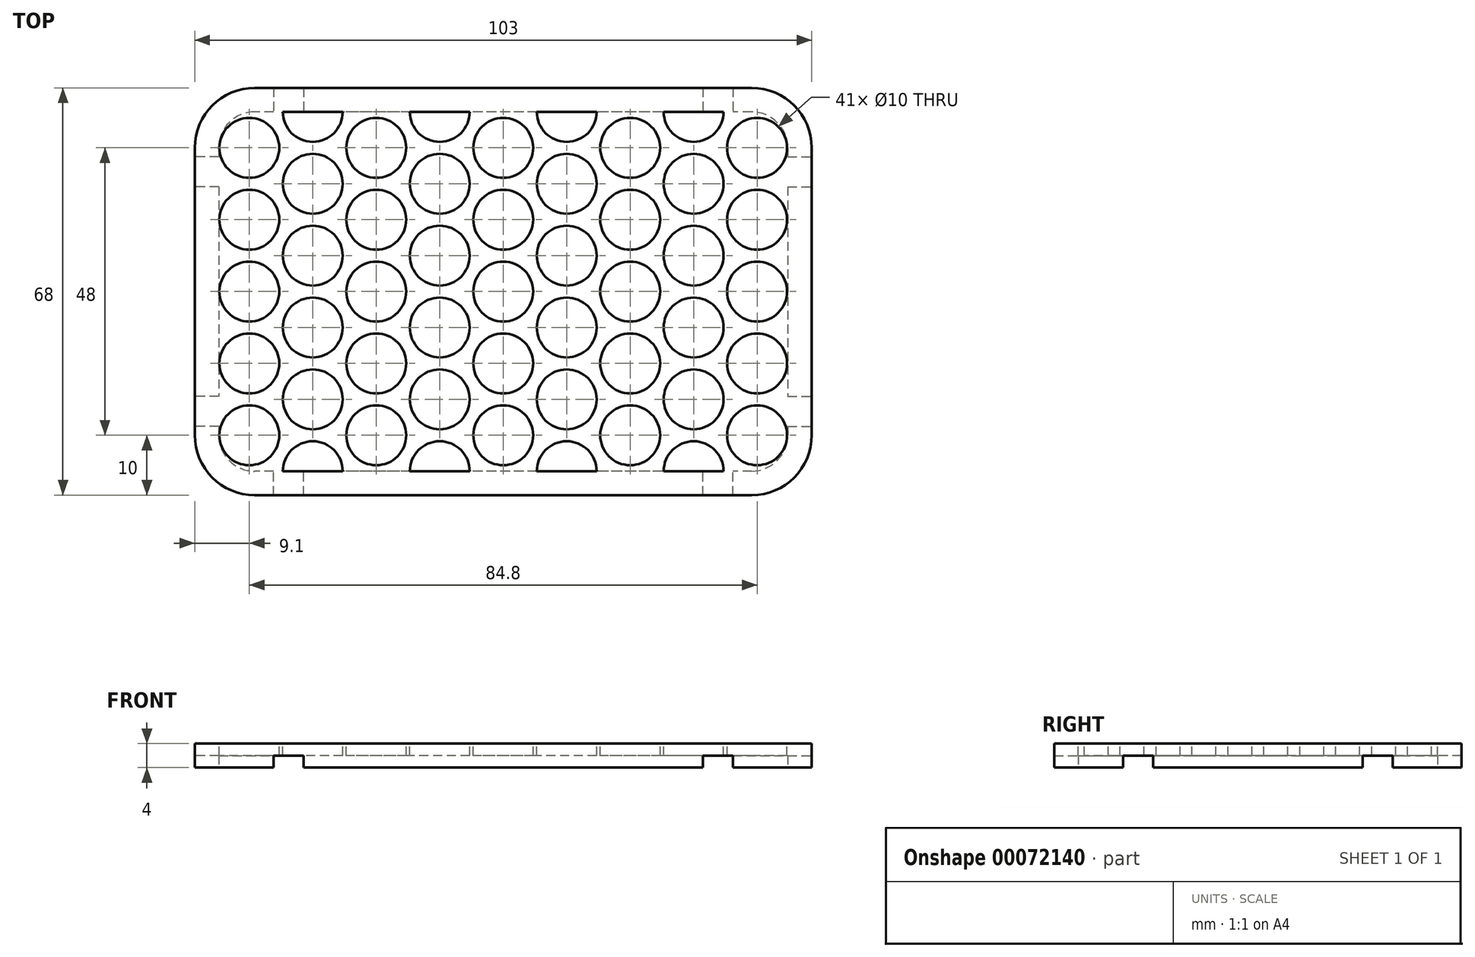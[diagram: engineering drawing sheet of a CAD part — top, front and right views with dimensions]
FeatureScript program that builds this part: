
annotation { "Feature Type Name" : "Feature", "Feature Type Description" : "" }
export const myFeature = defineFeature(function(context is Context, id is Id, definition is map)
    precondition{}
    {
        {
            var Q0;
            Q0=qCreatedBy(makeId("Top.planeOp"),FACE);
            var sketch = newSketch(context, id + "F0", { "sketchPlane" : qUnion([Q0])});
            skLineSegment(sketch, "E0.rect.bottom", {"start": v(41.5, 34) * mm, "end": v(-41.5, 34) * mm});
            skLineSegment(sketch, "E0.rect.top", {"start": v(41.5, -34) * mm, "end": v(-41.5, -34) * mm});
            skLineSegment(sketch, "E0.rect.left", {"start": v(51.5, 24) * mm, "end": v(51.5, -24) * mm});
            skLineSegment(sketch, "E0.rect.right", {"start": v(-51.5, 24) * mm, "end": v(-51.5, -24) * mm});
            skPoint(sketch, "E0.rect.middle", {"position": v(0, 0) * mm});
            skPoint(sketch, "E1.visualSharp", {"position": v(-51.5, 34) * mm});
            skArc(sketch, "E1.filletArc", {"start": v(-41.5, 34) * mm, "mid": v(-48.57, 31.07) * mm, "end": v(-51.5, 24) * mm});
            skPoint(sketch, "E2.visualSharp", {"position": v(51.5, 34) * mm});
            skArc(sketch, "E2.filletArc", {"start": v(51.5, 24) * mm, "mid": v(48.57, 31.07) * mm, "end": v(41.5, 34) * mm});
            skPoint(sketch, "E3.visualSharp", {"position": v(51.5, -34) * mm});
            skArc(sketch, "E3.filletArc", {"start": v(41.5, -34) * mm, "mid": v(48.57, -31.07) * mm, "end": v(51.5, -24) * mm});
            skPoint(sketch, "E4.visualSharp", {"position": v(-51.5, -34) * mm});
            skArc(sketch, "E4.filletArc", {"start": v(-51.5, -24) * mm, "mid": v(-48.57, -31.07) * mm, "end": v(-41.5, -34) * mm});
            skArc(sketch, "E5.0", {"start": v(47.5, 24) * mm, "mid": v(45.74, 28.24) * mm, "end": v(41.5, 30) * mm});
            skLineSegment(sketch, "E5.1", {"start": v(47.5, 24) * mm, "end": v(47.5, -24) * mm});
            skLineSegment(sketch, "E5.2", {"start": v(41.5, 30) * mm, "end": v(-41.5, 30) * mm});
            skArc(sketch, "E5.3", {"start": v(41.5, -30) * mm, "mid": v(45.74, -28.24) * mm, "end": v(47.5, -24) * mm});
            skArc(sketch, "E5.4", {"start": v(-41.5, 30) * mm, "mid": v(-45.74, 28.24) * mm, "end": v(-47.5, 24) * mm});
            skLineSegment(sketch, "E5.5", {"start": v(-47.5, 24) * mm, "end": v(-47.5, -24) * mm});
            skArc(sketch, "E5.6", {"start": v(-47.5, -24) * mm, "mid": v(-45.74, -28.24) * mm, "end": v(-41.5, -30) * mm});
            skLineSegment(sketch, "E5.7", {"start": v(41.5, -30) * mm, "end": v(-41.5, -30) * mm});
            skSolve(sketch);
        }
        {
            var Q0;
            Q0=makeQuery(id+"F0.imprint","IMPRINT",FACE,{"disambiguationData":[TD([[makeQuery(id+"F0.imprint","IMPRINT",EDGE,{"derivedFrom":sQuery(id+"F0.wireOp",EDGE,"E0.rect.bottom")}),1.0]])]});
            extrude(context, id + "F1", {"entities" : qUnion([Q0]), "depth" : 4 * mm});
        }
        {
            var Q0;
            Q0=makeQuery(id+"F1.opExtrude","CAP_FACE",FACE,{"disambiguationData":[OSD([sQuery(id+"F0.wireOp",EDGE,"E0.rect.bottom"),sQuery(id+"F0.wireOp",EDGE,"E0.rect.top"),sQuery(id+"F0.wireOp",EDGE,"E0.rect.left"),sQuery(id+"F0.wireOp",EDGE,"E0.rect.right"),sQuery(id+"F0.wireOp",EDGE,"E1.filletArc"),sQuery(id+"F0.wireOp",EDGE,"E2.filletArc"),sQuery(id+"F0.wireOp",EDGE,"E3.filletArc"),sQuery(id+"F0.wireOp",EDGE,"E4.filletArc"),sQuery(id+"F0.wireOp",EDGE,"E5.0"),sQuery(id+"F0.wireOp",EDGE,"E5.1"),sQuery(id+"F0.wireOp",EDGE,"E5.2"),sQuery(id+"F0.wireOp",EDGE,"E5.3"),sQuery(id+"F0.wireOp",EDGE,"E5.4"),sQuery(id+"F0.wireOp",EDGE,"E5.5"),sQuery(id+"F0.wireOp",EDGE,"E5.6"),sQuery(id+"F0.wireOp",EDGE,"E5.7")])],"isStart":false});
            var sketch = newSketch(context, id + "F2", { "sketchPlane" : qUnion([Q0])});
            skLineSegment(sketch, "E6.0", {"start": v(41.5, 30) * mm, "end": v(-41.5, 30) * mm});
            skArc(sketch, "E7.0", {"start": v(-41.5, 30) * mm, "mid": v(-45.74, 28.24) * mm, "end": v(-47.5, 24) * mm});
            skLineSegment(sketch, "E8.0", {"start": v(-47.5, 24) * mm, "end": v(-47.5, -24) * mm});
            skArc(sketch, "E9.0", {"start": v(-47.5, -24) * mm, "mid": v(-45.74, -28.24) * mm, "end": v(-41.5, -30) * mm});
            skLineSegment(sketch, "E10.0", {"start": v(41.5, -30) * mm, "end": v(-41.5, -30) * mm});
            skArc(sketch, "E11.0", {"start": v(41.5, -30) * mm, "mid": v(45.74, -28.24) * mm, "end": v(47.5, -24) * mm});
            skLineSegment(sketch, "E12.0", {"start": v(47.5, 24) * mm, "end": v(47.5, -24) * mm});
            skArc(sketch, "E13.0", {"start": v(47.5, 24) * mm, "mid": v(45.74, 28.24) * mm, "end": v(41.5, 30) * mm});
            skLineSegment(sketch, "E14.0", {"start": v(41.5, 34) * mm, "end": v(-41.5, 34) * mm});
            skArc(sketch, "E15.0", {"start": v(-41.5, 34) * mm, "mid": v(-48.57, 31.07) * mm, "end": v(-51.5, 24) * mm});
            skLineSegment(sketch, "E16.0", {"start": v(-51.5, 24) * mm, "end": v(-51.5, -24) * mm});
            skArc(sketch, "E17.0", {"start": v(51.5, 24) * mm, "mid": v(48.57, 31.07) * mm, "end": v(41.5, 34) * mm});
            skLineSegment(sketch, "E18.0", {"start": v(51.5, 24) * mm, "end": v(51.5, -24) * mm});
            skArc(sketch, "E19.0", {"start": v(41.5, -34) * mm, "mid": v(48.57, -31.07) * mm, "end": v(51.5, -24) * mm});
            skLineSegment(sketch, "E20.0", {"start": v(41.5, -34) * mm, "end": v(-41.5, -34) * mm});
            skArc(sketch, "E21.0", {"start": v(-51.5, -24) * mm, "mid": v(-48.57, -31.07) * mm, "end": v(-41.5, -34) * mm});
            skSolve(sketch);
        }
        {
            var Q0;
            Q0 = qSketchRegion(id + "F2", true);
            extrude(context, id + "F3", {"entities" : qUnion([Q0]), "oppositeDirection" : true, "depth" : 2 * mm});
        }
        {
            var Q0;
            Q0=makeQuery(id+"F3.opExtrude","SWEPT_BODY",BODY,{"disambiguationData":[OSD([sQuery(id+"F2.wireOp",EDGE,"E6.0"),sQuery(id+"F2.wireOp",EDGE,"E7.0"),sQuery(id+"F2.wireOp",EDGE,"E8.0"),sQuery(id+"F2.wireOp",EDGE,"E9.0"),sQuery(id+"F2.wireOp",EDGE,"E10.0"),sQuery(id+"F2.wireOp",EDGE,"E11.0"),sQuery(id+"F2.wireOp",EDGE,"E12.0"),sQuery(id+"F2.wireOp",EDGE,"E13.0")])]});
            deleteBodies(context, id + "F4", {"entities" : qUnion([Q0])});
        }
        {
            var Q0;
            Q0=makeQuery(id+"F2.imprint","IMPRINT",FACE,{"disambiguationData":[TD([[makeQuery(id+"F2.imprint","IMPRINT",EDGE,{"derivedFrom":sQuery(id+"F2.wireOp",EDGE,"E6.0")}),1.0]])]});
            var Q1;
            Q1=makeQuery(id+"F2.imprint","IMPRINT",FACE,{"disambiguationData":[TD([[makeQuery(id+"F2.imprint","IMPRINT",EDGE,{"derivedFrom":sQuery(id+"F2.wireOp",EDGE,"E6.0")}),-1.0]])]});
            extrude(context, id + "F5", {"entities" : qUnion([Q0, Q1]), "operationType" : NewBodyOperationType.ADD, "oppositeDirection" : true, "depth" : 2 * mm});
        }
        {
            var Q0;
            Q0=makeQuery(id+"F1.opExtrude","CAP_FACE",FACE,{"disambiguationData":[OSD([sQuery(id+"F0.wireOp",EDGE,"E0.rect.bottom"),sQuery(id+"F0.wireOp",EDGE,"E0.rect.top"),sQuery(id+"F0.wireOp",EDGE,"E0.rect.left"),sQuery(id+"F0.wireOp",EDGE,"E0.rect.right"),sQuery(id+"F0.wireOp",EDGE,"E1.filletArc"),sQuery(id+"F0.wireOp",EDGE,"E2.filletArc"),sQuery(id+"F0.wireOp",EDGE,"E3.filletArc"),sQuery(id+"F0.wireOp",EDGE,"E4.filletArc"),sQuery(id+"F0.wireOp",EDGE,"E5.0"),sQuery(id+"F0.wireOp",EDGE,"E5.1"),sQuery(id+"F0.wireOp",EDGE,"E5.2"),sQuery(id+"F0.wireOp",EDGE,"E5.3"),sQuery(id+"F0.wireOp",EDGE,"E5.4"),sQuery(id+"F0.wireOp",EDGE,"E5.5"),sQuery(id+"F0.wireOp",EDGE,"E5.6"),sQuery(id+"F0.wireOp",EDGE,"E5.7")])],"isStart":true});
            var sketch = newSketch(context, id + "F6", { "sketchPlane" : qUnion([Q0])});
            skLineSegment(sketch, "E22", {"start": v(0, 34) * mm, "end": v(0, 30) * mm, "construction": true});
            skLineSegment(sketch, "E23", {"start": v(-47.5, 0) * mm, "end": v(-51.5, 0) * mm, "construction": true});
            skLineSegment(sketch, "E24", {"start": v(0, 32) * mm, "end": v(-41.58, 32) * mm, "construction": true});
            skPoint(sketch, "E25", {"position": v(-35.85, 32) * mm});
            skLineSegment(sketch, "E26.rect.bottom", {"start": v(-33.35, 34) * mm, "end": v(-38.35, 34) * mm});
            skLineSegment(sketch, "E26.rect.top", {"start": v(-33.35, 30) * mm, "end": v(-38.35, 30) * mm});
            skLineSegment(sketch, "E26.rect.left", {"start": v(-33.35, 34) * mm, "end": v(-33.35, 30) * mm});
            skLineSegment(sketch, "E26.rect.right", {"start": v(-38.35, 34) * mm, "end": v(-38.35, 30) * mm});
            skLineSegment(sketch, "E27.MirrorCS", {"start": v(33.35, 30) * mm, "end": v(38.35, 30) * mm});
            skLineSegment(sketch, "E28.MirrorCS", {"start": v(33.35, 34) * mm, "end": v(33.35, 30) * mm});
            skLineSegment(sketch, "E29.MirrorCS", {"start": v(33.35, 34) * mm, "end": v(38.35, 34) * mm});
            skLineSegment(sketch, "E30.MirrorCS", {"start": v(38.35, 34) * mm, "end": v(38.35, 30) * mm});
            skLineSegment(sketch, "E31.MirrorCS", {"start": v(-38.35, -34) * mm, "end": v(-38.35, -30) * mm});
            skLineSegment(sketch, "E32.MirrorCS", {"start": v(-33.35, -34) * mm, "end": v(-38.35, -34) * mm});
            skLineSegment(sketch, "E33.MirrorCS", {"start": v(-33.35, -34) * mm, "end": v(-33.35, -30) * mm});
            skLineSegment(sketch, "E34.MirrorCS", {"start": v(-33.35, -30) * mm, "end": v(-38.35, -30) * mm});
            skLineSegment(sketch, "E35.MirrorCS", {"start": v(33.35, -34) * mm, "end": v(33.35, -30) * mm});
            skLineSegment(sketch, "E36.MirrorCS", {"start": v(33.35, -34) * mm, "end": v(38.35, -34) * mm});
            skLineSegment(sketch, "E37.MirrorCS", {"start": v(38.35, -34) * mm, "end": v(38.35, -30) * mm});
            skLineSegment(sketch, "E38.MirrorCS", {"start": v(33.35, -30) * mm, "end": v(38.35, -30) * mm});
            skLineSegment(sketch, "E39", {"start": v(-49.5, 0) * mm, "end": v(-49.5, 23.73) * mm, "construction": true});
            skPoint(sketch, "E40", {"position": v(-49.5, 20) * mm});
            skLineSegment(sketch, "E41.rect.bottom", {"start": v(-47.5, 22.5) * mm, "end": v(-51.5, 22.5) * mm});
            skLineSegment(sketch, "E41.rect.top", {"start": v(-47.5, 17.5) * mm, "end": v(-51.5, 17.5) * mm});
            skLineSegment(sketch, "E41.rect.left", {"start": v(-47.5, 22.5) * mm, "end": v(-47.5, 17.5) * mm});
            skLineSegment(sketch, "E41.rect.right", {"start": v(-51.5, 22.5) * mm, "end": v(-51.5, 17.5) * mm});
            skLineSegment(sketch, "E42.MirrorCS", {"start": v(-47.5, -17.5) * mm, "end": v(-51.5, -17.5) * mm});
            skLineSegment(sketch, "E43.MirrorCS", {"start": v(-51.5, -22.5) * mm, "end": v(-51.5, -17.5) * mm});
            skLineSegment(sketch, "E44.MirrorCS", {"start": v(-47.5, -22.5) * mm, "end": v(-51.5, -22.5) * mm});
            skLineSegment(sketch, "E45.MirrorCS", {"start": v(-47.5, -22.5) * mm, "end": v(-47.5, -17.5) * mm});
            skLineSegment(sketch, "E46.MirrorCS", {"start": v(47.5, -17.5) * mm, "end": v(51.5, -17.5) * mm});
            skLineSegment(sketch, "E47.MirrorCS", {"start": v(47.5, -22.5) * mm, "end": v(47.5, -17.5) * mm});
            skLineSegment(sketch, "E48.MirrorCS", {"start": v(47.5, -22.5) * mm, "end": v(51.5, -22.5) * mm});
            skLineSegment(sketch, "E49.MirrorCS", {"start": v(51.5, -22.5) * mm, "end": v(51.5, -17.5) * mm});
            skLineSegment(sketch, "E50.MirrorCS", {"start": v(47.5, 17.5) * mm, "end": v(51.5, 17.5) * mm});
            skLineSegment(sketch, "E51.MirrorCS", {"start": v(47.5, 22.5) * mm, "end": v(47.5, 17.5) * mm});
            skLineSegment(sketch, "E52.MirrorCS", {"start": v(47.5, 22.5) * mm, "end": v(51.5, 22.5) * mm});
            skLineSegment(sketch, "E53.MirrorCS", {"start": v(51.5, 22.5) * mm, "end": v(51.5, 17.5) * mm});
            skSolve(sketch);
        }
        {
            var Q0;
            Q0 = qSketchRegion(id + "F6", true);
            extrude(context, id + "F7", {"entities" : qUnion([Q0]), "operationType" : NewBodyOperationType.REMOVE, "oppositeDirection" : true, "depth" : 2 * mm});
        }
        {
            var Q0;
            Q0=makeQuery(id+"F5.boolean.opBoolean","MERGE",FACE,{"derivedFrom":[makeQuery(id+"F1.opExtrude","CAP_FACE",FACE,{"disambiguationData":[OSD([sQuery(id+"F0.wireOp",EDGE,"E0.rect.bottom"),sQuery(id+"F0.wireOp",EDGE,"E0.rect.top"),sQuery(id+"F0.wireOp",EDGE,"E0.rect.left"),sQuery(id+"F0.wireOp",EDGE,"E0.rect.right"),sQuery(id+"F0.wireOp",EDGE,"E1.filletArc"),sQuery(id+"F0.wireOp",EDGE,"E2.filletArc"),sQuery(id+"F0.wireOp",EDGE,"E3.filletArc"),sQuery(id+"F0.wireOp",EDGE,"E4.filletArc"),sQuery(id+"F0.wireOp",EDGE,"E5.0"),sQuery(id+"F0.wireOp",EDGE,"E5.1"),sQuery(id+"F0.wireOp",EDGE,"E5.2"),sQuery(id+"F0.wireOp",EDGE,"E5.3"),sQuery(id+"F0.wireOp",EDGE,"E5.4"),sQuery(id+"F0.wireOp",EDGE,"E5.5"),sQuery(id+"F0.wireOp",EDGE,"E5.6"),sQuery(id+"F0.wireOp",EDGE,"E5.7")])],"isStart":false}),makeQuery(id+"F5.opExtrude","CAP_FACE",FACE,{"disambiguationData":[OSD([sQuery(id+"F2.wireOp",EDGE,"E14.0"),sQuery(id+"F2.wireOp",EDGE,"E15.0"),sQuery(id+"F2.wireOp",EDGE,"E16.0"),sQuery(id+"F2.wireOp",EDGE,"E17.0"),sQuery(id+"F2.wireOp",EDGE,"E18.0"),sQuery(id+"F2.wireOp",EDGE,"E19.0"),sQuery(id+"F2.wireOp",EDGE,"E20.0"),sQuery(id+"F2.wireOp",EDGE,"E21.0")])],"isStart":true})]});
            var sketch = newSketch(context, id + "F8", { "sketchPlane" : qUnion([Q0])});
            skLineSegment(sketch, "E54.0", {"start": v(41.5, 30) * mm, "end": v(-41.5, 30) * mm});
            skLineSegment(sketch, "E55.0", {"start": v(-47.5, 24) * mm, "end": v(-47.5, -24) * mm});
            skArc(sketch, "E56.0", {"start": v(-41.5, 30) * mm, "mid": v(-45.74, 28.24) * mm, "end": v(-47.5, 24) * mm});
            skArc(sketch, "E57.0", {"start": v(-47.5, -24) * mm, "mid": v(-45.74, -28.24) * mm, "end": v(-41.5, -30) * mm});
            skLineSegment(sketch, "E58.0", {"start": v(41.5, -30) * mm, "end": v(-41.5, -30) * mm});
            skArc(sketch, "E59.0", {"start": v(41.5, -30) * mm, "mid": v(45.74, -28.24) * mm, "end": v(47.5, -24) * mm});
            skLineSegment(sketch, "E60.0", {"start": v(47.5, 24) * mm, "end": v(47.5, -24) * mm});
            skArc(sketch, "E61.0", {"start": v(47.5, 24) * mm, "mid": v(45.74, 28.24) * mm, "end": v(41.5, 30) * mm});
            skLineSegment(sketch, "E62", {"start": v(-42.4, 30) * mm, "end": v(-42.4, -30) * mm, "construction": true});
            skLineSegment(sketch, "E63", {"start": v(-47.5, 0) * mm, "end": v(47.5, 0) * mm, "construction": true});
            skPoint(sketch, "E64", {"position": v(-42.4, 0) * mm});
            skCircle(sketch, "E65", {"center": v(-42.4, 0) * mm, "radius": 5 * mm});
            skPoint(sketch, "E66", {"position": v(-42.4, 12) * mm});
            skCircle(sketch, "E67", {"center": v(-42.4, 12) * mm, "radius": 5 * mm});
            skPoint(sketch, "E68", {"position": v(-42.4, 24) * mm});
            skCircle(sketch, "E69", {"center": v(-42.4, 24) * mm, "radius": 5 * mm});
            skCircle(sketch, "E70.MirrorC", {"center": v(-42.4, -12) * mm, "radius": 5 * mm});
            skCircle(sketch, "E71.MirrorC", {"center": v(-42.4, -24) * mm, "radius": 5 * mm});
            skLineSegment(sketch, "E72", {"start": v(-31.8, 30) * mm, "end": v(-31.8, -30) * mm, "construction": true});
            skArc(sketch, "E73", {"start": v(-36.8, 30) * mm, "mid": v(-31.8, 25) * mm, "end": v(-26.8, 30) * mm});
            skPoint(sketch, "E74", {"position": v(-31.8, 18) * mm});
            skCircle(sketch, "E75", {"center": v(-31.8, 18) * mm, "radius": 5 * mm});
            skPoint(sketch, "E76", {"position": v(-31.8, 6) * mm});
            skCircle(sketch, "E77", {"center": v(-31.8, 6) * mm, "radius": 5 * mm});
            skCircle(sketch, "E78.MirrorC", {"center": v(-31.8, -6) * mm, "radius": 5 * mm});
            skCircle(sketch, "E79.MirrorC", {"center": v(-31.8, -18) * mm, "radius": 5 * mm});
            skArc(sketch, "E80.MirrorCS", {"start": v(-36.8, -30) * mm, "mid": v(-31.8, -25) * mm, "end": v(-26.8, -30) * mm});
            skCircle(sketch, "E81.MirrorC", {"center": v(-21.2, -12) * mm, "radius": 5 * mm});
            skCircle(sketch, "E82.MirrorC", {"center": v(-21.2, -24) * mm, "radius": 5 * mm});
            skCircle(sketch, "E83.MirrorC", {"center": v(-21.2, 12) * mm, "radius": 5 * mm});
            skCircle(sketch, "E84.MirrorC", {"center": v(-21.2, 24) * mm, "radius": 5 * mm});
            skLineSegment(sketch, "E85", {"start": v(-21.2, 24) * mm, "end": v(-21.2, -24) * mm, "construction": true});
            skCircle(sketch, "E86.MirrorC", {"center": v(-21.2, 0) * mm, "radius": 5 * mm});
            skCircle(sketch, "E87.MirrorC", {"center": v(-10.6, 18) * mm, "radius": 5 * mm});
            skArc(sketch, "E88.MirrorCS", {"start": v(-5.6, 30) * mm, "mid": v(-10.6, 25) * mm, "end": v(-15.6, 30) * mm});
            skCircle(sketch, "E89.MirrorC", {"center": v(-10.6, 6) * mm, "radius": 5 * mm});
            skCircle(sketch, "E90.MirrorC", {"center": v(-10.6, -6) * mm, "radius": 5 * mm});
            skCircle(sketch, "E91.MirrorC", {"center": v(-10.6, -18) * mm, "radius": 5 * mm});
            skArc(sketch, "E92.MirrorCS", {"start": v(-5.6, -30) * mm, "mid": v(-10.6, -25) * mm, "end": v(-15.6, -30) * mm});
            skLineSegment(sketch, "E93", {"start": v(-10.6, 30) * mm, "end": v(-10.6, -30) * mm, "construction": true});
            skCircle(sketch, "E94.MirrorC", {"center": v(0, 24) * mm, "radius": 5 * mm});
            skCircle(sketch, "E95.MirrorC", {"center": v(0, 12) * mm, "radius": 5 * mm});
            skCircle(sketch, "E96.MirrorC", {"center": v(0, 0) * mm, "radius": 5 * mm});
            skCircle(sketch, "E97.MirrorC", {"center": v(0, -12) * mm, "radius": 5 * mm});
            skCircle(sketch, "E98.MirrorC", {"center": v(0, -24) * mm, "radius": 5 * mm});
            skLineSegment(sketch, "E99", {"start": v(0, 24) * mm, "end": v(0, -24) * mm, "construction": true});
            skArc(sketch, "E100.MirrorCS", {"start": v(5.6, 30) * mm, "mid": v(10.6, 25) * mm, "end": v(15.6, 30) * mm});
            skCircle(sketch, "E101.MirrorC", {"center": v(10.6, 18) * mm, "radius": 5 * mm});
            skCircle(sketch, "E102.MirrorC", {"center": v(10.6, 6) * mm, "radius": 5 * mm});
            skCircle(sketch, "E103.MirrorC", {"center": v(10.6, -6) * mm, "radius": 5 * mm});
            skCircle(sketch, "E104.MirrorC", {"center": v(10.6, -18) * mm, "radius": 5 * mm});
            skArc(sketch, "E105.MirrorCS", {"start": v(5.6, -30) * mm, "mid": v(10.6, -25) * mm, "end": v(15.6, -30) * mm});
            skLineSegment(sketch, "E106", {"start": v(10.6, 30) * mm, "end": v(10.6, -30) * mm, "construction": true});
            skCircle(sketch, "E107.MirrorC", {"center": v(21.2, 24) * mm, "radius": 5 * mm});
            skCircle(sketch, "E108.MirrorC", {"center": v(21.2, 12) * mm, "radius": 5 * mm});
            skCircle(sketch, "E109.MirrorC", {"center": v(21.2, 0) * mm, "radius": 5 * mm});
            skCircle(sketch, "E110.MirrorC", {"center": v(21.2, -12) * mm, "radius": 5 * mm});
            skCircle(sketch, "E111.MirrorC", {"center": v(21.2, -24) * mm, "radius": 5 * mm});
            skLineSegment(sketch, "E112", {"start": v(21.2, 24) * mm, "end": v(21.2, -24) * mm, "construction": true});
            skArc(sketch, "E113.MirrorCS", {"start": v(36.8, 30) * mm, "mid": v(31.8, 25) * mm, "end": v(26.8, 30) * mm});
            skCircle(sketch, "E114.MirrorC", {"center": v(31.8, 18) * mm, "radius": 5 * mm});
            skCircle(sketch, "E115.MirrorC", {"center": v(31.8, 6) * mm, "radius": 5 * mm});
            skCircle(sketch, "E116.MirrorC", {"center": v(31.8, -6) * mm, "radius": 5 * mm});
            skCircle(sketch, "E117.MirrorC", {"center": v(31.8, -18) * mm, "radius": 5 * mm});
            skArc(sketch, "E118.MirrorCS", {"start": v(36.8, -30) * mm, "mid": v(31.8, -25) * mm, "end": v(26.8, -30) * mm});
            skLineSegment(sketch, "E119", {"start": v(31.8, 30) * mm, "end": v(31.8, -30) * mm, "construction": true});
            skCircle(sketch, "E120.MirrorC", {"center": v(42.4, 24) * mm, "radius": 5 * mm});
            skCircle(sketch, "E121.MirrorC", {"center": v(42.4, 12) * mm, "radius": 5 * mm});
            skCircle(sketch, "E122.MirrorC", {"center": v(42.4, 0) * mm, "radius": 5 * mm});
            skCircle(sketch, "E123.MirrorC", {"center": v(42.4, -12) * mm, "radius": 5 * mm});
            skCircle(sketch, "E124.MirrorC", {"center": v(42.4, -24) * mm, "radius": 5 * mm});
            skLineSegment(sketch, "E125", {"start": v(-36.8, 30) * mm, "end": v(-26.8, 30) * mm});
            skLineSegment(sketch, "E126", {"start": v(-15.6, 30) * mm, "end": v(-5.6, 30) * mm});
            skLineSegment(sketch, "E127", {"start": v(5.6, 30) * mm, "end": v(15.6, 30) * mm});
            skLineSegment(sketch, "E128", {"start": v(26.8, 30) * mm, "end": v(36.8, 30) * mm});
            skLineSegment(sketch, "E129", {"start": v(-36.8, -30) * mm, "end": v(-26.8, -30) * mm});
            skLineSegment(sketch, "E130", {"start": v(-15.6, -30) * mm, "end": v(-5.6, -30) * mm});
            skLineSegment(sketch, "E131", {"start": v(5.6, -30) * mm, "end": v(15.6, -30) * mm});
            skLineSegment(sketch, "E132", {"start": v(26.8, -30) * mm, "end": v(36.8, -30) * mm});
            skSolve(sketch);
        }
        {
            var Q0;
            Q0=makeQuery(id+"F5.boolean.opBoolean","MERGE",FACE,{"derivedFrom":[makeQuery(id+"F1.opExtrude","CAP_FACE",FACE,{"disambiguationData":[OSD([sQuery(id+"F0.wireOp",EDGE,"E0.rect.bottom"),sQuery(id+"F0.wireOp",EDGE,"E0.rect.top"),sQuery(id+"F0.wireOp",EDGE,"E0.rect.left"),sQuery(id+"F0.wireOp",EDGE,"E0.rect.right"),sQuery(id+"F0.wireOp",EDGE,"E1.filletArc"),sQuery(id+"F0.wireOp",EDGE,"E2.filletArc"),sQuery(id+"F0.wireOp",EDGE,"E3.filletArc"),sQuery(id+"F0.wireOp",EDGE,"E4.filletArc"),sQuery(id+"F0.wireOp",EDGE,"E5.0"),sQuery(id+"F0.wireOp",EDGE,"E5.1"),sQuery(id+"F0.wireOp",EDGE,"E5.2"),sQuery(id+"F0.wireOp",EDGE,"E5.3"),sQuery(id+"F0.wireOp",EDGE,"E5.4"),sQuery(id+"F0.wireOp",EDGE,"E5.5"),sQuery(id+"F0.wireOp",EDGE,"E5.6"),sQuery(id+"F0.wireOp",EDGE,"E5.7")])],"isStart":false}),makeQuery(id+"F5.opExtrude","CAP_FACE",FACE,{"disambiguationData":[OSD([sQuery(id+"F2.wireOp",EDGE,"E14.0"),sQuery(id+"F2.wireOp",EDGE,"E15.0"),sQuery(id+"F2.wireOp",EDGE,"E16.0"),sQuery(id+"F2.wireOp",EDGE,"E17.0"),sQuery(id+"F2.wireOp",EDGE,"E18.0"),sQuery(id+"F2.wireOp",EDGE,"E19.0"),sQuery(id+"F2.wireOp",EDGE,"E20.0"),sQuery(id+"F2.wireOp",EDGE,"E21.0")])],"isStart":true})]});
            var sketch = newSketch(context, id + "F9", { "sketchPlane" : qUnion([Q0])});
            skCircle(sketch, "E133.0", {"center": v(-42.4, 24) * mm, "radius": 5 * mm});
            skArc(sketch, "E134.0", {"start": v(-36.8, 30) * mm, "mid": v(-31.8, 25) * mm, "end": v(-26.8, 30) * mm});
            skCircle(sketch, "E135.0", {"center": v(-31.8, 18) * mm, "radius": 5 * mm});
            skCircle(sketch, "E136.0", {"center": v(-42.4, 12) * mm, "radius": 5 * mm});
            skCircle(sketch, "E137.0", {"center": v(-42.4, 0) * mm, "radius": 5 * mm});
            skCircle(sketch, "E138.0", {"center": v(-31.8, 6) * mm, "radius": 5 * mm});
            skCircle(sketch, "E139.0", {"center": v(-31.8, -6) * mm, "radius": 5 * mm});
            skCircle(sketch, "E140.0", {"center": v(-42.4, -12) * mm, "radius": 5 * mm});
            skCircle(sketch, "E141.0", {"center": v(-42.4, -24) * mm, "radius": 5 * mm});
            skCircle(sketch, "E142.0", {"center": v(-31.8, -18) * mm, "radius": 5 * mm});
            skArc(sketch, "E143.0", {"start": v(-36.8, -30) * mm, "mid": v(-31.8, -25) * mm, "end": v(-26.8, -30) * mm});
            skCircle(sketch, "E144.0", {"center": v(-21.2, -24) * mm, "radius": 5 * mm});
            skCircle(sketch, "E145.0", {"center": v(-21.2, -12) * mm, "radius": 5 * mm});
            skCircle(sketch, "E146.0", {"center": v(-21.2, 0) * mm, "radius": 5 * mm});
            skCircle(sketch, "E147.0", {"center": v(-21.2, 12) * mm, "radius": 5 * mm});
            skCircle(sketch, "E148.0", {"center": v(-21.2, 24) * mm, "radius": 5 * mm});
            skArc(sketch, "E149.0", {"start": v(-5.6, 30) * mm, "mid": v(-10.6, 25) * mm, "end": v(-15.6, 30) * mm});
            skCircle(sketch, "E150.0", {"center": v(-10.6, 18) * mm, "radius": 5 * mm});
            skCircle(sketch, "E151.0", {"center": v(-10.6, 6) * mm, "radius": 5 * mm});
            skCircle(sketch, "E152.0", {"center": v(-10.6, -6) * mm, "radius": 5 * mm});
            skCircle(sketch, "E153.0", {"center": v(-10.6, -18) * mm, "radius": 5 * mm});
            skArc(sketch, "E154.0", {"start": v(-5.6, -30) * mm, "mid": v(-10.6, -25) * mm, "end": v(-15.6, -30) * mm});
            skCircle(sketch, "E155.0", {"center": v(0, -24) * mm, "radius": 5 * mm});
            skCircle(sketch, "E156.0", {"center": v(0, -12) * mm, "radius": 5 * mm});
            skCircle(sketch, "E157.0", {"center": v(0, 0) * mm, "radius": 5 * mm});
            skCircle(sketch, "E158.0", {"center": v(0, 12) * mm, "radius": 5 * mm});
            skCircle(sketch, "E159.0", {"center": v(0, 24) * mm, "radius": 5 * mm});
            skArc(sketch, "E160.0", {"start": v(5.6, 30) * mm, "mid": v(10.6, 25) * mm, "end": v(15.6, 30) * mm});
            skCircle(sketch, "E161.0", {"center": v(10.6, 18) * mm, "radius": 5 * mm});
            skCircle(sketch, "E162.0", {"center": v(10.6, 6) * mm, "radius": 5 * mm});
            skCircle(sketch, "E163.0", {"center": v(10.6, -6) * mm, "radius": 5 * mm});
            skCircle(sketch, "E164.0", {"center": v(10.6, -18) * mm, "radius": 5 * mm});
            skArc(sketch, "E165.0", {"start": v(5.6, -30) * mm, "mid": v(10.6, -25) * mm, "end": v(15.6, -30) * mm});
            skCircle(sketch, "E166.0", {"center": v(21.2, -24) * mm, "radius": 5 * mm});
            skCircle(sketch, "E167.0", {"center": v(21.2, -12) * mm, "radius": 5 * mm});
            skCircle(sketch, "E168.0", {"center": v(21.2, 0) * mm, "radius": 5 * mm});
            skCircle(sketch, "E169.0", {"center": v(21.2, 12) * mm, "radius": 5 * mm});
            skCircle(sketch, "E170.0", {"center": v(21.2, 24) * mm, "radius": 5 * mm});
            skArc(sketch, "E171.0", {"start": v(36.8, 30) * mm, "mid": v(31.8, 25) * mm, "end": v(26.8, 30) * mm});
            skCircle(sketch, "E172.0", {"center": v(31.8, 18) * mm, "radius": 5 * mm});
            skCircle(sketch, "E173.0", {"center": v(31.8, 6) * mm, "radius": 5 * mm});
            skCircle(sketch, "E174.0", {"center": v(31.8, -6) * mm, "radius": 5 * mm});
            skCircle(sketch, "E175.0", {"center": v(31.8, -18) * mm, "radius": 5 * mm});
            skArc(sketch, "E176.0", {"start": v(36.8, -30) * mm, "mid": v(31.8, -25) * mm, "end": v(26.8, -30) * mm});
            skCircle(sketch, "E177.0", {"center": v(42.4, -24) * mm, "radius": 5 * mm});
            skCircle(sketch, "E178.0", {"center": v(42.4, -12) * mm, "radius": 5 * mm});
            skCircle(sketch, "E179.0", {"center": v(42.4, 0) * mm, "radius": 5 * mm});
            skCircle(sketch, "E180.0", {"center": v(42.4, 12) * mm, "radius": 5 * mm});
            skCircle(sketch, "E181.0", {"center": v(42.4, 24) * mm, "radius": 5 * mm});
            skLineSegment(sketch, "E182", {"start": v(-36.8, 30) * mm, "end": v(-26.8, 30) * mm});
            skLineSegment(sketch, "E183", {"start": v(-15.6, 30) * mm, "end": v(-5.6, 30) * mm});
            skLineSegment(sketch, "E184", {"start": v(5.6, 30) * mm, "end": v(15.6, 30) * mm});
            skLineSegment(sketch, "E185", {"start": v(26.8, 30) * mm, "end": v(36.8, 30) * mm});
            skLineSegment(sketch, "E186", {"start": v(-36.8, -30) * mm, "end": v(-26.8, -30) * mm});
            skLineSegment(sketch, "E187", {"start": v(-15.6, -30) * mm, "end": v(-5.6, -30) * mm});
            skLineSegment(sketch, "E188", {"start": v(5.6, -30) * mm, "end": v(15.6, -30) * mm});
            skLineSegment(sketch, "E189", {"start": v(26.8, -30) * mm, "end": v(36.8, -30) * mm});
            skSolve(sketch);
        }
        {
            var Q0;
            Q0 = qSketchRegion(id + "F9", true);
            extrude(context, id + "F10", {"entities" : qUnion([Q0]), "operationType" : NewBodyOperationType.REMOVE, "endBound" : BoundingType.THROUGH_ALL, "oppositeDirection" : true, "depth" : 25 * mm});
        }
    });
